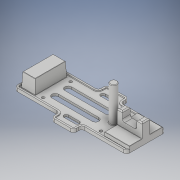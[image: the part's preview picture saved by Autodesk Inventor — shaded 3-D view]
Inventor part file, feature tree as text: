
AUTODESK INVENTOR PART (.ipt)
format: ipt  version: 2017 (Build 210142000, 142)  size: 373,760 bytes
history: native  units: in
note: dims shown in document units (in); Inventor stores cm internally (conversion verified against a paired STEP export)
features: extrude x7, sketch x6, fillet x4, draft x1, projected_geometry x1
ambient origin geometry x8: Origin, YZ Plane, XZ Plane, XY Plane, X Axis, Y Axis, Z Axis, Center Point
bodies: Solid1 (feature_tree)
feature tree (19):
  extrude  "Base"  Depth=2.7559in
  extrude  "Chassis"  Depth=0.1575in
  draft  "FaceDraft2"
  extrude  "Step"  Depth=1.7717in
  extrude  "RearWheels"  Depth=5.7874in
  extrude  "Edge"  Depth=1.7717in
  fillet  "Fillet1mm"  Radius=2.3622in
  fillet  "Fillet4mm"  Radius=0.2756in
  fillet  "Fillet3"  Radius=0.1969in
  extrude  "Pin"  Depth=0.315in
  fillet  "Fillet4"  Radius=0.6102in
  extrude  "Extrusion7"  Depth=0.315in
  sketch  "Sketch2"  dims[d0=7.9921in d1=2.7559in]
  sketch  "Sketch3"  dims[d4=0.1575in d5=0.0in d6=0.9646in]
  sketch  "Sketch4"  dims[d7=2.2441in d8=1.7717in]
  sketch  "Sketch5"  dims[d9=2.3622in d10=5.7874in]
  projected_geometry  "Projected Loop2"
  sketch  "Sketch6"  dims[d12=0.9843in d13=0.0in d15=1.7717in d16=2.3622in d17=0.2756in d18=0.0in d19=0.1969in]
  sketch  "Sketch7"  dims[d20=0.9843in d21=1.0433in d22=0.6102in d23=1.7717in d24=0.3642in d25=0.5512in d26=0.0in d29=0.0787in d30=0.0in d31=0.0197in d32=0.1575in d33=0.0787in d37=0.0172in d38=5.9055in d40=0.2362in d41=0.4921in d42=1.7913in d43=0.8957in d44=1.4173in d45=2.4803in d46=0.0in d47=0.0394in d48=1.5748in d49=3.937in d50=0.1969in d51=0.1181in d52=0.1969in d56=2.3622in d60=0.9843in d62=0.4724in d63=0.3937in d64=0.0in d65=0.1969in d66=1.7717in d67=0.9843in d68=0.3937in d69=0.315in]
